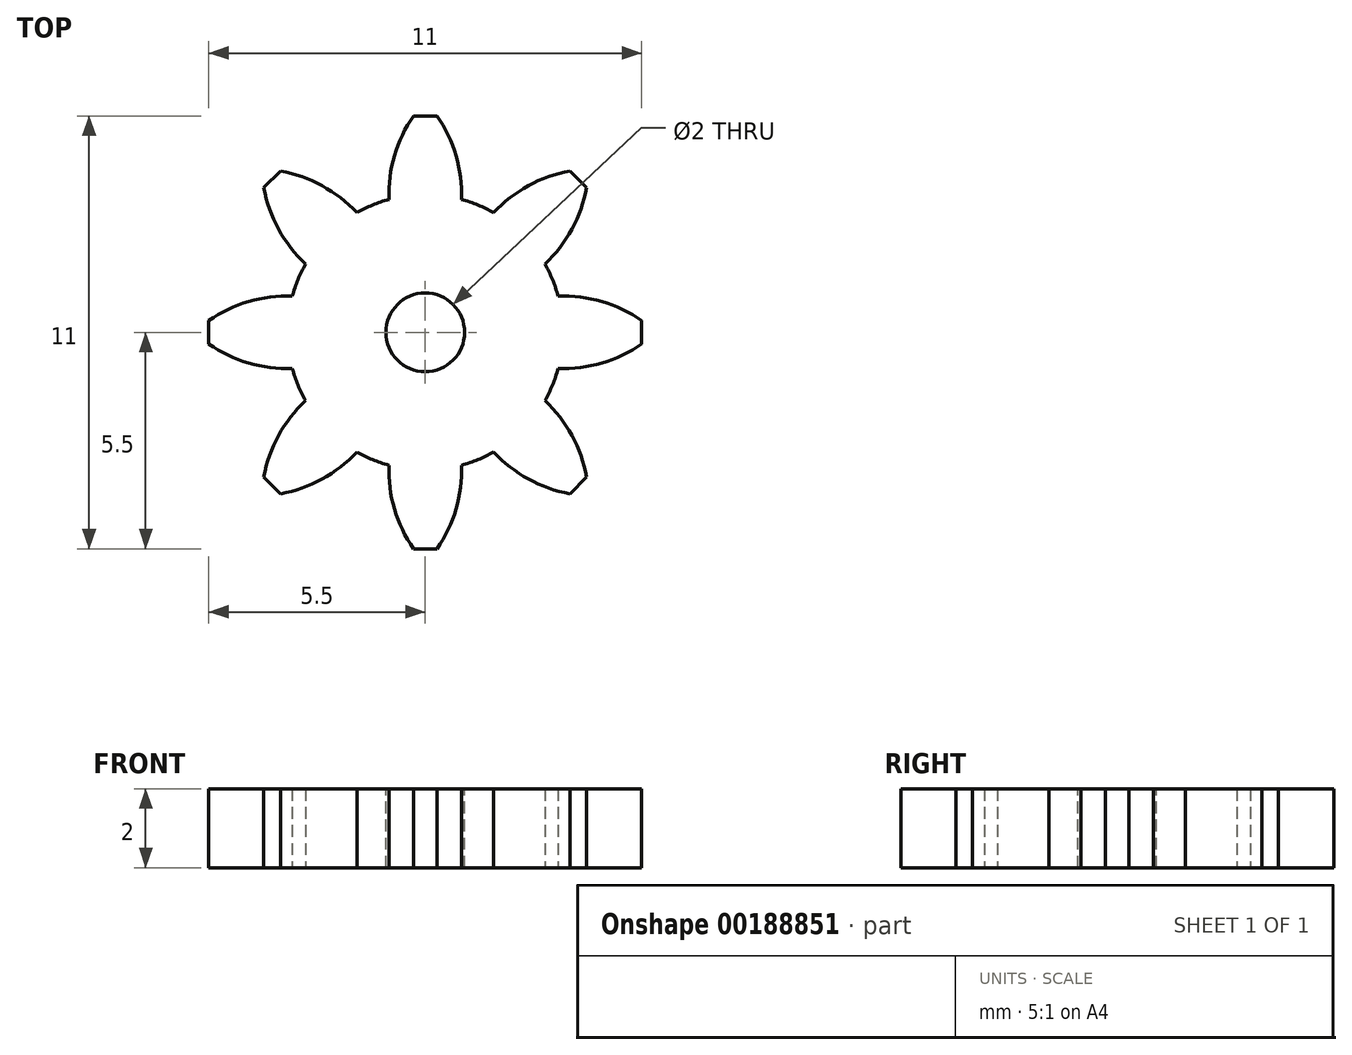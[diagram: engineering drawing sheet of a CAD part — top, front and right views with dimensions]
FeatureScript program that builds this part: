
annotation { "Feature Type Name" : "Feature", "Feature Type Description" : "" }
export const myFeature = defineFeature(function(context is Context, id is Id, definition is map)
    precondition{}
    {
        {
            var Q0;
            Q0=qCreatedBy(makeId("Top.planeOp"),FACE);
            var sketch = newSketch(context, id + "F0", { "sketchPlane" : qUnion([Q0])});
            skCircle(sketch, "E0", {"center": v(0, 0) * mm, "radius": 3.5 * mm});
            skLineSegment(sketch, "E1", {"start": v(0, 0) * mm, "end": v(0, 3.5) * mm, "construction": true});
            skLineSegment(sketch, "E2", {"start": v(0, 5.5) * mm, "end": v(-0.3, 5.5) * mm});
            skArc(sketch, "E3", {"start": v(-0.3, 5.5) * mm, "mid": v(-0.78, 4.49) * mm, "end": v(-0.92, 3.38) * mm});
            skLineSegment(sketch, "E4.MirrorCS", {"start": v(0, 5.5) * mm, "end": v(0.3, 5.5) * mm});
            skArc(sketch, "E5.MirrorCS", {"start": v(0.3, 5.5) * mm, "mid": v(0.78, 4.49) * mm, "end": v(0.92, 3.38) * mm});
            skArc(sketch, "E6.1.0", {"start": v(-4.1, 3.68) * mm, "mid": v(-3.73, 2.62) * mm, "end": v(-3.04, 1.74) * mm});
            skLineSegment(sketch, "E6.1.1", {"start": v(-3.89, 3.89) * mm, "end": v(-4.1, 3.68) * mm});
            skLineSegment(sketch, "E6.1.2", {"start": v(-3.89, 3.89) * mm, "end": v(-3.68, 4.1) * mm});
            skArc(sketch, "E6.1.3", {"start": v(-3.68, 4.1) * mm, "mid": v(-2.62, 3.73) * mm, "end": v(-1.74, 3.04) * mm});
            skArc(sketch, "E6.2.0", {"start": v(-5.5, -0.3) * mm, "mid": v(-4.49, -0.78) * mm, "end": v(-3.38, -0.92) * mm});
            skLineSegment(sketch, "E6.2.1", {"start": v(-5.5, 0) * mm, "end": v(-5.5, -0.3) * mm});
            skLineSegment(sketch, "E6.2.2", {"start": v(-5.5, 0) * mm, "end": v(-5.5, 0.3) * mm});
            skArc(sketch, "E6.2.3", {"start": v(-5.5, 0.3) * mm, "mid": v(-4.49, 0.78) * mm, "end": v(-3.38, 0.92) * mm});
            skArc(sketch, "E6.3.0", {"start": v(-3.68, -4.1) * mm, "mid": v(-2.62, -3.73) * mm, "end": v(-1.74, -3.04) * mm});
            skLineSegment(sketch, "E6.3.1", {"start": v(-3.89, -3.89) * mm, "end": v(-3.68, -4.1) * mm});
            skLineSegment(sketch, "E6.3.2", {"start": v(-3.89, -3.89) * mm, "end": v(-4.1, -3.68) * mm});
            skArc(sketch, "E6.3.3", {"start": v(-4.1, -3.68) * mm, "mid": v(-3.73, -2.62) * mm, "end": v(-3.04, -1.74) * mm});
            skArc(sketch, "E6.4.0", {"start": v(0.3, -5.5) * mm, "mid": v(0.78, -4.49) * mm, "end": v(0.92, -3.38) * mm});
            skLineSegment(sketch, "E6.4.1", {"start": v(0, -5.5) * mm, "end": v(0.3, -5.5) * mm});
            skLineSegment(sketch, "E6.4.2", {"start": v(0, -5.5) * mm, "end": v(-0.3, -5.5) * mm});
            skArc(sketch, "E6.4.3", {"start": v(-0.3, -5.5) * mm, "mid": v(-0.78, -4.49) * mm, "end": v(-0.92, -3.38) * mm});
            skArc(sketch, "E6.5.0", {"start": v(4.1, -3.68) * mm, "mid": v(3.73, -2.62) * mm, "end": v(3.04, -1.74) * mm});
            skLineSegment(sketch, "E6.5.1", {"start": v(3.89, -3.89) * mm, "end": v(4.1, -3.68) * mm});
            skLineSegment(sketch, "E6.5.2", {"start": v(3.89, -3.89) * mm, "end": v(3.68, -4.1) * mm});
            skArc(sketch, "E6.5.3", {"start": v(3.68, -4.1) * mm, "mid": v(2.62, -3.73) * mm, "end": v(1.74, -3.04) * mm});
            skArc(sketch, "E6.6.0", {"start": v(5.5, 0.3) * mm, "mid": v(4.49, 0.78) * mm, "end": v(3.38, 0.92) * mm});
            skLineSegment(sketch, "E6.6.1", {"start": v(5.5, 0) * mm, "end": v(5.5, 0.3) * mm});
            skLineSegment(sketch, "E6.6.2", {"start": v(5.5, 0) * mm, "end": v(5.5, -0.3) * mm});
            skArc(sketch, "E6.6.3", {"start": v(5.5, -0.3) * mm, "mid": v(4.49, -0.78) * mm, "end": v(3.38, -0.92) * mm});
            skArc(sketch, "E6.7.0", {"start": v(3.68, 4.1) * mm, "mid": v(2.62, 3.73) * mm, "end": v(1.74, 3.04) * mm});
            skLineSegment(sketch, "E6.7.1", {"start": v(3.89, 3.89) * mm, "end": v(3.68, 4.1) * mm});
            skLineSegment(sketch, "E6.7.2", {"start": v(3.89, 3.89) * mm, "end": v(4.1, 3.68) * mm});
            skArc(sketch, "E6.7.3", {"start": v(4.1, 3.68) * mm, "mid": v(3.73, 2.62) * mm, "end": v(3.04, 1.74) * mm});
            skSolve(sketch);
        }
        {
            var Q0;
            Q0=qSketchRegion(id+"F0",true);
            extrude(context, id + "F1", {"entities" : qUnion([Q0]), "depth" : 2 * mm});
        }
        {
            var Q0;
            Q0=makeQuery(id+"F1.opExtrude","CAP_FACE",FACE,{"disambiguationData":[OSD([sQuery(id+"F0.wireOp",EDGE,"E0"),sQuery(id+"F0.wireOp",EDGE,"E2"),sQuery(id+"F0.wireOp",EDGE,"E3"),sQuery(id+"F0.wireOp",EDGE,"E4.MirrorCS"),sQuery(id+"F0.wireOp",EDGE,"E5.MirrorCS"),sQuery(id+"F0.wireOp",EDGE,"E6.1.0"),sQuery(id+"F0.wireOp",EDGE,"E6.1.1"),sQuery(id+"F0.wireOp",EDGE,"E6.1.2"),sQuery(id+"F0.wireOp",EDGE,"E6.1.3"),sQuery(id+"F0.wireOp",EDGE,"E6.2.0"),sQuery(id+"F0.wireOp",EDGE,"E6.2.1"),sQuery(id+"F0.wireOp",EDGE,"E6.2.2"),sQuery(id+"F0.wireOp",EDGE,"E6.2.3"),sQuery(id+"F0.wireOp",EDGE,"E6.3.0"),sQuery(id+"F0.wireOp",EDGE,"E6.3.1"),sQuery(id+"F0.wireOp",EDGE,"E6.3.2"),sQuery(id+"F0.wireOp",EDGE,"E6.3.3"),sQuery(id+"F0.wireOp",EDGE,"E6.4.0"),sQuery(id+"F0.wireOp",EDGE,"E6.4.1"),sQuery(id+"F0.wireOp",EDGE,"E6.4.2"),sQuery(id+"F0.wireOp",EDGE,"E6.4.3"),sQuery(id+"F0.wireOp",EDGE,"E6.5.0"),sQuery(id+"F0.wireOp",EDGE,"E6.5.1"),sQuery(id+"F0.wireOp",EDGE,"E6.5.2"),sQuery(id+"F0.wireOp",EDGE,"E6.5.3"),sQuery(id+"F0.wireOp",EDGE,"E6.6.0"),sQuery(id+"F0.wireOp",EDGE,"E6.6.1"),sQuery(id+"F0.wireOp",EDGE,"E6.6.2"),sQuery(id+"F0.wireOp",EDGE,"E6.6.3"),sQuery(id+"F0.wireOp",EDGE,"E6.7.0"),sQuery(id+"F0.wireOp",EDGE,"E6.7.1"),sQuery(id+"F0.wireOp",EDGE,"E6.7.2"),sQuery(id+"F0.wireOp",EDGE,"E6.7.3"),sQuery(id+"F0.wireOp",EDGE,"E6.8.0"),sQuery(id+"F0.wireOp",EDGE,"E6.8.1"),sQuery(id+"F0.wireOp",EDGE,"E6.8.2"),sQuery(id+"F0.wireOp",EDGE,"E6.8.3"),sQuery(id+"F0.wireOp",EDGE,"E6.9.0"),sQuery(id+"F0.wireOp",EDGE,"E6.9.1"),sQuery(id+"F0.wireOp",EDGE,"E6.9.2"),sQuery(id+"F0.wireOp",EDGE,"E6.9.3"),sQuery(id+"F0.wireOp",EDGE,"E6.10.0"),sQuery(id+"F0.wireOp",EDGE,"E6.10.1"),sQuery(id+"F0.wireOp",EDGE,"E6.10.2"),sQuery(id+"F0.wireOp",EDGE,"E6.10.3"),sQuery(id+"F0.wireOp",EDGE,"E6.11.0"),sQuery(id+"F0.wireOp",EDGE,"E6.11.1"),sQuery(id+"F0.wireOp",EDGE,"E6.11.2"),sQuery(id+"F0.wireOp",EDGE,"E6.11.3"),sQuery(id+"F0.wireOp",EDGE,"E6.12.0"),sQuery(id+"F0.wireOp",EDGE,"E6.12.1"),sQuery(id+"F0.wireOp",EDGE,"E6.12.2"),sQuery(id+"F0.wireOp",EDGE,"E6.12.3"),sQuery(id+"F0.wireOp",EDGE,"E6.13.0"),sQuery(id+"F0.wireOp",EDGE,"E6.13.1"),sQuery(id+"F0.wireOp",EDGE,"E6.13.2"),sQuery(id+"F0.wireOp",EDGE,"E6.13.3"),sQuery(id+"F0.wireOp",EDGE,"E6.14.0"),sQuery(id+"F0.wireOp",EDGE,"E6.14.1"),sQuery(id+"F0.wireOp",EDGE,"E6.14.2"),sQuery(id+"F0.wireOp",EDGE,"E6.14.3"),sQuery(id+"F0.wireOp",EDGE,"E6.15.0"),sQuery(id+"F0.wireOp",EDGE,"E6.15.1"),sQuery(id+"F0.wireOp",EDGE,"E6.15.2"),sQuery(id+"F0.wireOp",EDGE,"E6.15.3")])],"isStart":false});
            var sketch = newSketch(context, id + "F2", { "sketchPlane" : qUnion([Q0])});
            skCircle(sketch, "E7", {"center": v(0, 0) * mm, "radius": 1 * mm});
            skSolve(sketch);
        }
        {
            var Q0;
            Q0=qSketchRegion(id+"F2",true);
            extrude(context, id + "F3", {"entities" : qUnion([Q0]), "operationType" : NewBodyOperationType.REMOVE, "endBound" : BoundingType.THROUGH_ALL, "oppositeDirection" : true, "depth" : 25 * mm});
        }
    });
